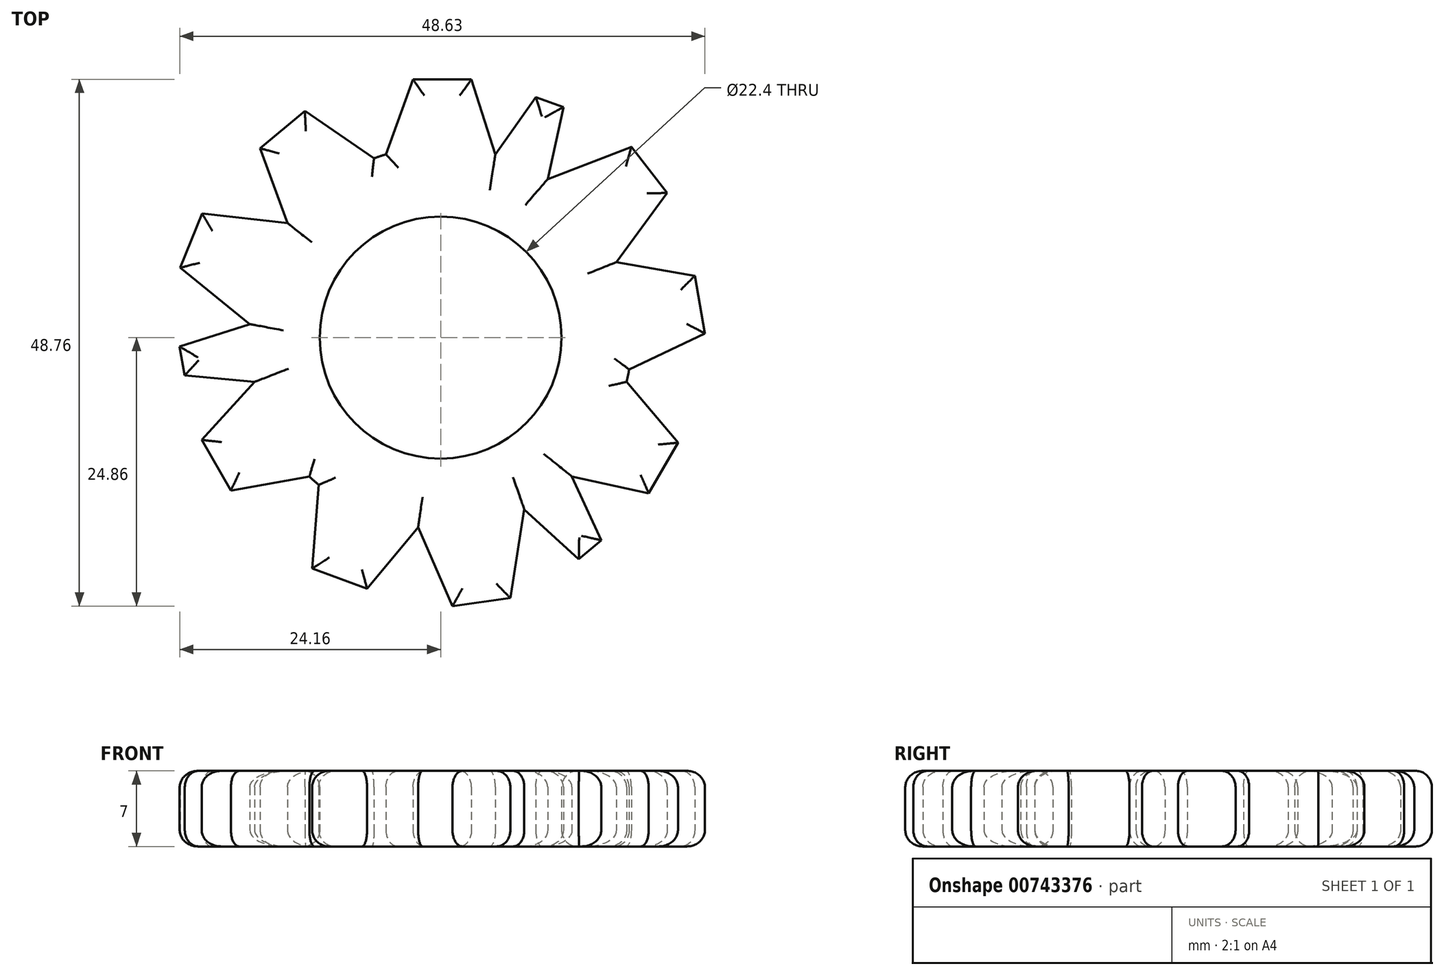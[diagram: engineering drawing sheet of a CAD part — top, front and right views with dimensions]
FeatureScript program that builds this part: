
annotation { "Feature Type Name" : "Feature", "Feature Type Description" : "" }
export const myFeature = defineFeature(function(context is Context, id is Id, definition is map)
    precondition{}
    {
        {
            var Q0;
            Q0=qCreatedBy(makeId("Top.planeOp"),FACE);
            var sketch = newSketch(context, id + "F0", { "sketchPlane" : qUnion([Q0])});
            skCircle(sketch, "E0", {"center": v(0, 0) * mm, "radius": 11.2 * mm});
            skLineSegment(sketch, "E1", {"start": v(-5.06, 16.96) * mm, "end": v(-2.55, 23.9) * mm});
            skLineSegment(sketch, "E2", {"start": v(-2.55, 23.9) * mm, "end": v(2.86, 23.9) * mm});
            skLineSegment(sketch, "E3", {"start": v(2.86, 23.9) * mm, "end": v(5.06, 16.96) * mm});
            skLineSegment(sketch, "E4.1.0", {"start": v(-22.12, -9.47) * mm, "end": v(-17.22, -4.1) * mm});
            skLineSegment(sketch, "E4.1.1", {"start": v(-12.16, -12.86) * mm, "end": v(-19.42, -14.16) * mm});
            skLineSegment(sketch, "E4.1.2", {"start": v(-19.42, -14.16) * mm, "end": v(-22.12, -9.47) * mm});
            skLineSegment(sketch, "E4.2.0", {"start": v(19.27, -14.42) * mm, "end": v(12.16, -12.86) * mm});
            skLineSegment(sketch, "E4.2.1", {"start": v(17.22, -4.1) * mm, "end": v(21.97, -9.74) * mm});
            skLineSegment(sketch, "E4.2.2", {"start": v(21.97, -9.74) * mm, "end": v(19.27, -14.42) * mm});
            skLineSegment(sketch, "E5", {"start": v(16.26, 6.98) * mm, "end": v(23.53, 5.72) * mm});
            skLineSegment(sketch, "E6", {"start": v(23.53, 5.72) * mm, "end": v(24.47, 0.4) * mm});
            skLineSegment(sketch, "E7", {"start": v(24.47, 0.4) * mm, "end": v(17.45, -2.95) * mm});
            skLineSegment(sketch, "E8.1.0", {"start": v(-14.18, 10.6) * mm, "end": v(-16.72, 17.52) * mm});
            skLineSegment(sketch, "E8.1.1", {"start": v(-16.72, 17.52) * mm, "end": v(-12.57, 21) * mm});
            skLineSegment(sketch, "E8.1.2", {"start": v(-12.57, 21) * mm, "end": v(-6.17, 16.59) * mm});
            skLineSegment(sketch, "E8.2.0", {"start": v(-2.08, -17.58) * mm, "end": v(-6.81, -23.24) * mm});
            skLineSegment(sketch, "E8.2.1", {"start": v(-6.81, -23.24) * mm, "end": v(-11.9, -21.39) * mm});
            skLineSegment(sketch, "E8.2.2", {"start": v(-11.9, -21.39) * mm, "end": v(-11.28, -13.64) * mm});
            skLineSegment(sketch, "E9", {"start": v(-17.66, 1.25) * mm, "end": v(-24.11, 6.46) * mm});
            skLineSegment(sketch, "E10", {"start": v(-24.11, 6.46) * mm, "end": v(-22.08, 11.48) * mm});
            skLineSegment(sketch, "E11", {"start": v(-22.08, 11.48) * mm, "end": v(-14.18, 10.6) * mm});
            skLineSegment(sketch, "E12.1.0", {"start": v(1.1, -24.86) * mm, "end": v(-2.08, -17.58) * mm});
            skLineSegment(sketch, "E12.1.1", {"start": v(7.75, -15.91) * mm, "end": v(6.46, -24.11) * mm});
            skLineSegment(sketch, "E12.1.2", {"start": v(6.46, -24.11) * mm, "end": v(1.1, -24.86) * mm});
            skLineSegment(sketch, "E12.2.0", {"start": v(20.98, 13.38) * mm, "end": v(16.26, 6.98) * mm});
            skLineSegment(sketch, "E12.2.1", {"start": v(9.9, 14.67) * mm, "end": v(17.65, 17.65) * mm});
            skLineSegment(sketch, "E12.2.2", {"start": v(17.65, 17.65) * mm, "end": v(20.98, 13.38) * mm});
            skLineSegment(sketch, "E13", {"start": v(5.06, 16.96) * mm, "end": v(8.81, 22.26) * mm});
            skLineSegment(sketch, "E14", {"start": v(8.81, 22.26) * mm, "end": v(11.37, 21.34) * mm});
            skLineSegment(sketch, "E15", {"start": v(11.37, 21.34) * mm, "end": v(9.9, 14.67) * mm});
            skLineSegment(sketch, "E16.1.0", {"start": v(-23.69, -3.5) * mm, "end": v(-24.16, -0.82) * mm});
            skLineSegment(sketch, "E16.1.1", {"start": v(-17.22, -4.1) * mm, "end": v(-23.69, -3.5) * mm});
            skLineSegment(sketch, "E16.1.2", {"start": v(-24.16, -0.82) * mm, "end": v(-17.66, 1.25) * mm});
            skLineSegment(sketch, "E16.2.0", {"start": v(14.87, -18.76) * mm, "end": v(12.8, -20.51) * mm});
            skLineSegment(sketch, "E16.2.1", {"start": v(12.16, -12.86) * mm, "end": v(14.87, -18.76) * mm});
            skLineSegment(sketch, "E16.2.2", {"start": v(12.8, -20.51) * mm, "end": v(7.75, -15.91) * mm});
            skArc(sketch, "E17.trimOffspring", {"start": v(-5.06, 16.96) * mm, "mid": v(-5.62, 16.78) * mm, "end": v(-6.17, 16.59) * mm});
            skArc(sketch, "E18.trimOffspring", {"start": v(17.22, -4.1) * mm, "mid": v(17.35, -3.53) * mm, "end": v(17.45, -2.95) * mm});
            skArc(sketch, "E19.trimOffspring", {"start": v(-12.16, -12.86) * mm, "mid": v(-11.73, -13.26) * mm, "end": v(-11.28, -13.64) * mm});
            skSolve(sketch);
        }
        {
            var Q0;
            Q0=makeQuery(id+"F0.imprint","IMPRINT",FACE,{"disambiguationData":[TD([[makeQuery(id+"F0.imprint","IMPRINT",EDGE,{"derivedFrom":sQuery(id+"F0.wireOp",EDGE,"E0")}),-1.0]])]});
            extrude(context, id + "F1", {"entities" : qUnion([Q0]), "depth" : 7 * mm, "offsetDistance" : 25 * mm});
        }
        {
            var Q0;
            Q0=makeQuery(id+"F1.opExtrude","CAP_FACE",FACE,{"disambiguationData":[OSD([sQuery(id+"F0.wireOp",EDGE,"E0"),sQuery(id+"F0.wireOp",EDGE,"E1"),sQuery(id+"F0.wireOp",EDGE,"E2"),sQuery(id+"F0.wireOp",EDGE,"E3"),sQuery(id+"F0.wireOp",EDGE,"E4.1.0"),sQuery(id+"F0.wireOp",EDGE,"E4.1.1"),sQuery(id+"F0.wireOp",EDGE,"E4.1.2"),sQuery(id+"F0.wireOp",EDGE,"E4.2.0"),sQuery(id+"F0.wireOp",EDGE,"E4.2.1"),sQuery(id+"F0.wireOp",EDGE,"E4.2.2"),sQuery(id+"F0.wireOp",EDGE,"E5"),sQuery(id+"F0.wireOp",EDGE,"E6"),sQuery(id+"F0.wireOp",EDGE,"E7"),sQuery(id+"F0.wireOp",EDGE,"E8.1.0"),sQuery(id+"F0.wireOp",EDGE,"E8.1.1"),sQuery(id+"F0.wireOp",EDGE,"E8.1.2"),sQuery(id+"F0.wireOp",EDGE,"E8.2.0"),sQuery(id+"F0.wireOp",EDGE,"E8.2.1"),sQuery(id+"F0.wireOp",EDGE,"E8.2.2"),sQuery(id+"F0.wireOp",EDGE,"E9"),sQuery(id+"F0.wireOp",EDGE,"E10"),sQuery(id+"F0.wireOp",EDGE,"E11"),sQuery(id+"F0.wireOp",EDGE,"E12.1.0"),sQuery(id+"F0.wireOp",EDGE,"E12.1.1"),sQuery(id+"F0.wireOp",EDGE,"E12.1.2"),sQuery(id+"F0.wireOp",EDGE,"E12.2.0"),sQuery(id+"F0.wireOp",EDGE,"E12.2.1"),sQuery(id+"F0.wireOp",EDGE,"E12.2.2"),sQuery(id+"F0.wireOp",EDGE,"E13"),sQuery(id+"F0.wireOp",EDGE,"E14"),sQuery(id+"F0.wireOp",EDGE,"E15"),sQuery(id+"F0.wireOp",EDGE,"E16.1.0"),sQuery(id+"F0.wireOp",EDGE,"E16.1.1"),sQuery(id+"F0.wireOp",EDGE,"E16.1.2"),sQuery(id+"F0.wireOp",EDGE,"E16.2.0"),sQuery(id+"F0.wireOp",EDGE,"E16.2.1"),sQuery(id+"F0.wireOp",EDGE,"E16.2.2"),sQuery(id+"F0.wireOp",EDGE,"E17.trimOffspring"),sQuery(id+"F0.wireOp",EDGE,"E18.trimOffspring"),sQuery(id+"F0.wireOp",EDGE,"E19.trimOffspring")])],"isStart":true});
            var Q1;
            Q1=makeQuery(id+"F1.opExtrude","CAP_FACE",FACE,{"disambiguationData":[OSD([sQuery(id+"F0.wireOp",EDGE,"E0"),sQuery(id+"F0.wireOp",EDGE,"E1"),sQuery(id+"F0.wireOp",EDGE,"E2"),sQuery(id+"F0.wireOp",EDGE,"E3"),sQuery(id+"F0.wireOp",EDGE,"E4.1.0"),sQuery(id+"F0.wireOp",EDGE,"E4.1.1"),sQuery(id+"F0.wireOp",EDGE,"E4.1.2"),sQuery(id+"F0.wireOp",EDGE,"E4.2.0"),sQuery(id+"F0.wireOp",EDGE,"E4.2.1"),sQuery(id+"F0.wireOp",EDGE,"E4.2.2"),sQuery(id+"F0.wireOp",EDGE,"E5"),sQuery(id+"F0.wireOp",EDGE,"E6"),sQuery(id+"F0.wireOp",EDGE,"E7"),sQuery(id+"F0.wireOp",EDGE,"E8.1.0"),sQuery(id+"F0.wireOp",EDGE,"E8.1.1"),sQuery(id+"F0.wireOp",EDGE,"E8.1.2"),sQuery(id+"F0.wireOp",EDGE,"E8.2.0"),sQuery(id+"F0.wireOp",EDGE,"E8.2.1"),sQuery(id+"F0.wireOp",EDGE,"E8.2.2"),sQuery(id+"F0.wireOp",EDGE,"E9"),sQuery(id+"F0.wireOp",EDGE,"E10"),sQuery(id+"F0.wireOp",EDGE,"E11"),sQuery(id+"F0.wireOp",EDGE,"E12.1.0"),sQuery(id+"F0.wireOp",EDGE,"E12.1.1"),sQuery(id+"F0.wireOp",EDGE,"E12.1.2"),sQuery(id+"F0.wireOp",EDGE,"E12.2.0"),sQuery(id+"F0.wireOp",EDGE,"E12.2.1"),sQuery(id+"F0.wireOp",EDGE,"E12.2.2"),sQuery(id+"F0.wireOp",EDGE,"E13"),sQuery(id+"F0.wireOp",EDGE,"E14"),sQuery(id+"F0.wireOp",EDGE,"E15"),sQuery(id+"F0.wireOp",EDGE,"E16.1.0"),sQuery(id+"F0.wireOp",EDGE,"E16.1.1"),sQuery(id+"F0.wireOp",EDGE,"E16.1.2"),sQuery(id+"F0.wireOp",EDGE,"E16.2.0"),sQuery(id+"F0.wireOp",EDGE,"E16.2.1"),sQuery(id+"F0.wireOp",EDGE,"E16.2.2"),sQuery(id+"F0.wireOp",EDGE,"E17.trimOffspring"),sQuery(id+"F0.wireOp",EDGE,"E18.trimOffspring"),sQuery(id+"F0.wireOp",EDGE,"E19.trimOffspring")])],"isStart":false});
            fillet(context, id + "F2", {"entities" : qUnion([Q0, Q1]), "radius" : 1.5 * mm, "tangentPropagation" : true, "allowEdgeOverflow" : false});
        }
    });
